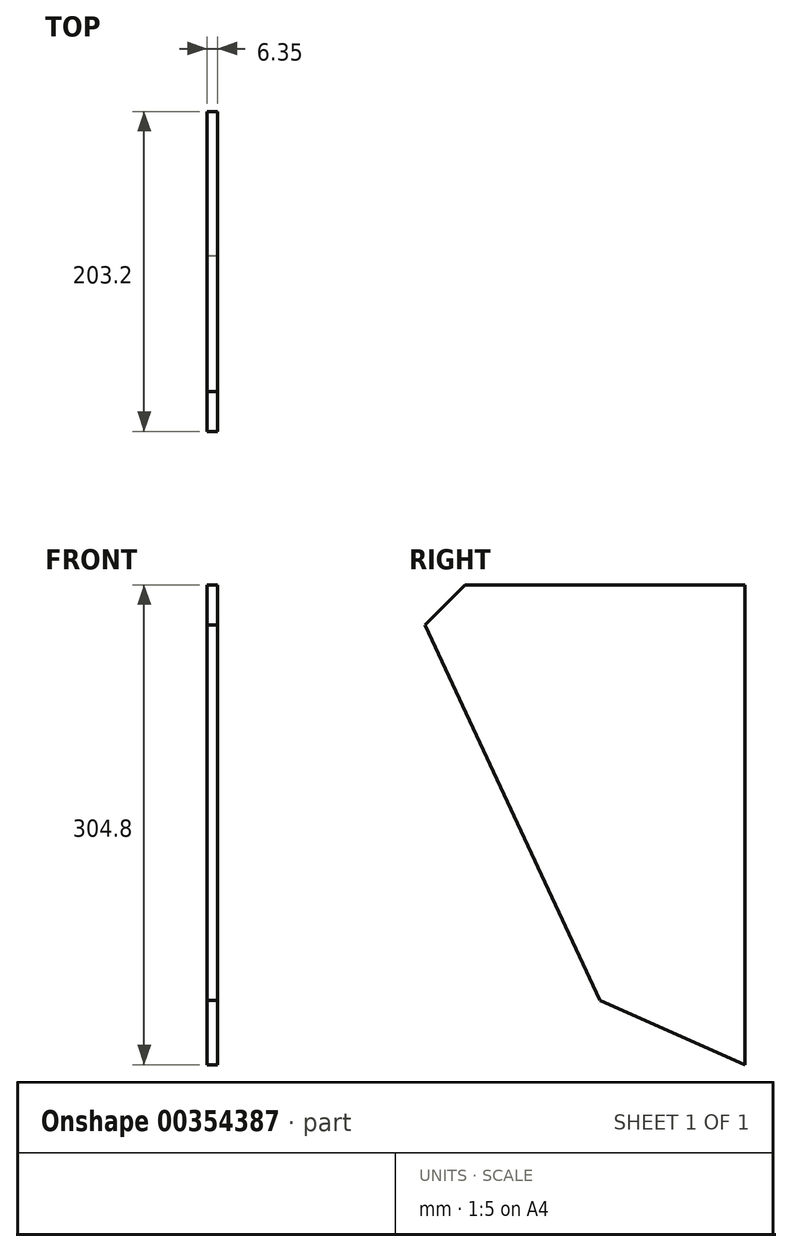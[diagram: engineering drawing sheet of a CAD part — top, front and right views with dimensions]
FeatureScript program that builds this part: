
annotation { "Feature Type Name" : "Feature", "Feature Type Description" : "" }
export const myFeature = defineFeature(function(context is Context, id is Id, definition is map)
    precondition{}
    {
        {
            var Q0;
            Q0=qCreatedBy(makeId("Right.planeOp"),FACE);
            var sketch = newSketch(context, id + "F0", { "sketchPlane" : qUnion([Q0])});
            skLineSegment(sketch, "E0.bottom", {"start": v(101.6, 152.4) * mm, "end": v(-76.2, 152.4) * mm});
            skLineSegment(sketch, "E0.left", {"start": v(101.6, 152.4) * mm, "end": v(101.6, -152.4) * mm});
            skPoint(sketch, "E0.middle", {"position": v(0, 0) * mm});
            skLineSegment(sketch, "E1", {"start": v(-101.6, 127) * mm, "end": v(-76.2, 152.4) * mm});
            skPoint(sketch, "E2.orphan", {"position": v(-101.6, 152.4) * mm});
            skLineSegment(sketch, "E3", {"start": v(-101.6, 127) * mm, "end": v(9.58, -111.43) * mm});
            skLineSegment(sketch, "E4", {"start": v(9.58, -111.43) * mm, "end": v(101.6, -152.4) * mm});
            skPoint(sketch, "E0.top.end.orphan", {"position": v(-101.6, -152.4) * mm});
            skLineSegment(sketch, "E5", {"start": v(-76.2, 152.4) * mm, "end": v(-101.6, 152.4) * mm, "construction": true});
            skLineSegment(sketch, "E6", {"start": v(-101.6, 127) * mm, "end": v(-101.6, 152.4) * mm, "construction": true});
            skLineSegment(sketch, "E7", {"start": v(-101.6, 127) * mm, "end": v(-101.6, -152.4) * mm, "construction": true});
            skLineSegment(sketch, "E8", {"start": v(-101.6, -152.4) * mm, "end": v(101.6, -152.4) * mm, "construction": true});
            skSolve(sketch);
        }
        {
            var Q0;
            Q0 = qSketchRegion(id + "F0", true);
            extrude(context, id + "F1", {"entities" : qUnion([Q0]), "depth" : 6.35 * mm});
        }
    });
